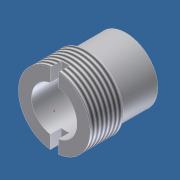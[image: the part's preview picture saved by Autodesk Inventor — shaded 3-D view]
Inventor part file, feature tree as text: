
AUTODESK INVENTOR PART (.ipt)
format: ipt  version: unknown  size: 200,192 bytes
history: native  units: in
note: dims shown in document units (in); Inventor stores cm internally (conversion verified against a paired STEP export)
features: sketch x4, revolve x1, hole x1, thread x1, plane x1, extrude x1
ambient origin geometry x8: Origin, YZ Plane, XZ Plane, XY Plane, X Axis, Y Axis, Z Axis, Center Point
bodies: Solid1 (feature_tree)
feature tree (9):
  revolve  "Revolution1"  Angle=90.0deg
  hole  "Hole1"  [1 undecoded]
  thread  "Thread1"  [1 undecoded]
  plane  "Work Plane1"
  extrude  "Extrusion1"  Depth=0.125in
  sketch  "Sketch4"  dims[d15=1.0in d16=0.0in d17=0.406in d18=0.359in d19=0.375in]
  sketch  "Sketch1"  dims[d0=0.812in d2=90.0deg]
  sketch  "Sketch2"  dims[d3=0.515in d4=0.75in d5=0.375in d6=0.25in d7=0.5635in d8=1.0in d9=0.0in d10=0.375in d11=0.437in d12=0.0465in]
  sketch  "Sketch3"  dims[d13=0.0465in d14=0.125in]
note: 2 required parameter values undecoded (feature->parameter linkage not recoverable at this tier; creation-order binding heuristic only, values carry confidence <= 0.55)
